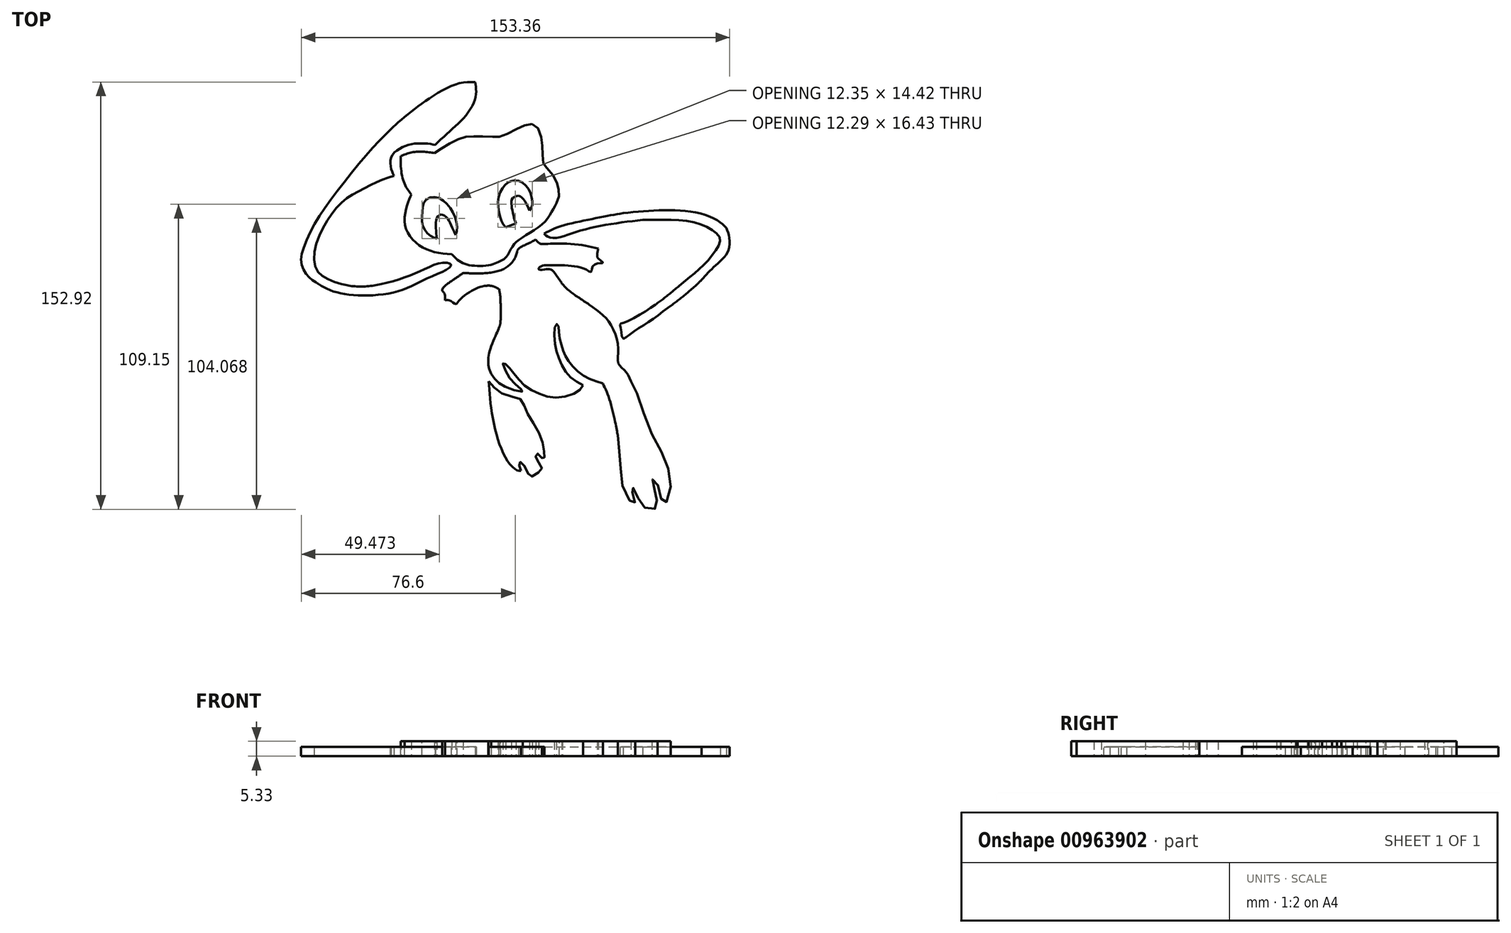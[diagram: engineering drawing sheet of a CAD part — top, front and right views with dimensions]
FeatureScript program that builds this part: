
annotation { "Feature Type Name" : "Feature", "Feature Type Description" : "" }
export const myFeature = defineFeature(function(context is Context, id is Id, definition is map)
    precondition{}
    {
        {
            var Q0;
            Q0=qCreatedBy(makeId("Top.planeOp"),FACE);
            var sketch = newSketch(context, id + "F0", { "sketchPlane" : qUnion([Q0])});
            skFitSpline(sketch, "E0", {"points": [v(-36.88, 36.08) * mm, v(-38.4, 38.25) * mm, v(-40.15, 42.6) * mm, v(-40.65, 48.33) * mm, v(-40.58, 49.85) * mm], "startDerivative": vector(-6.94, 9.09) * mm, "endDerivative": vector(0.6, 7.48) * mm});
            skFitSpline(sketch, "E1", {"points": [v(-40.58, 49.85) * mm, v(-38.04, 50.8) * mm, v(-34.93, 51.37) * mm, v(-31.38, 51.3) * mm, v(-28.55, 50.87) * mm], "startDerivative": vector(10.5, 4.31) * mm, "endDerivative": vector(11.28, -2.04) * mm});
            skFitSpline(sketch, "E2", {"points": [v(-28.55, 50.87) * mm, v(-24.87, 53.3) * mm, v(-19.99, 55.88) * mm, v(-16.36, 56.8) * mm, v(-12.2, 56.87) * mm, v(-6.98, 56.74) * mm, v(-4.41, 57) * mm, v(1, 59.57) * mm, v(4.83, 61.1) * mm, v(7.67, 60.76) * mm, v(9.65, 56.27) * mm, v(10.11, 52.11) * mm, v(10.44, 47.3) * mm, v(11.57, 45.71) * mm, v(14.54, 41.82) * mm, v(15.6, 38.91) * mm, v(16.05, 35.8) * mm, v(15.13, 32.97) * mm], "startDerivative": vector(55.8, 38.5) * mm, "endDerivative": vector(-24.9, -54.1) * mm});
            skFitSpline(sketch, "E3", {"points": [v(15.13, 32.97) * mm, v(13.23, 29.5) * mm, v(9.9, 25.32) * mm, v(3.54, 21.13) * mm, v(0, 18.38) * mm, v(-1.7, 15.62) * mm, v(-3.4, 13.15) * mm, v(-5.2, 12.2) * mm], "startDerivative": vector(-12.69, -24.26) * mm, "endDerivative": vector(-18.67, -6.95) * mm});
            skFitSpline(sketch, "E4", {"points": [v(-5.2, 12.2) * mm, v(-8.38, 10.92) * mm, v(-15.27, 10.68) * mm, v(-19.62, 12.2) * mm, v(-22.36, 14.64) * mm], "startDerivative": vector(-12.64, -6.7) * mm, "endDerivative": vector(-11.41, 11.76) * mm});
            skFitSpline(sketch, "E5", {"points": [v(-22.36, 14.64) * mm, v(-29.1, 15.62) * mm, v(-34.66, 18.38) * mm, v(-38.53, 23.3) * mm, v(-39.1, 28.91) * mm, v(-37.75, 33.9) * mm, v(-36.88, 36.08) * mm], "startDerivative": vector(-36.55, 3.17) * mm, "endDerivative": vector(7.3, 17.53) * mm});
            skFitSpline(sketch, "E6", {"points": [v(-27.74, 20.26) * mm, v(-28, 23.55) * mm, v(-27.97, 26.8) * mm, v(-27.14, 28.47) * mm, v(-25.9, 28.88) * mm, v(-24.15, 27.82) * mm, v(-22.83, 25.7) * mm, v(-21.65, 22.95) * mm, v(-20.94, 21.55) * mm], "startDerivative": vector(-1.85, 21.58) * mm, "endDerivative": vector(6.7, -12.08) * mm});
            skFitSpline(sketch, "E7", {"points": [v(-20.94, 21.55) * mm, v(-20.44, 24.42) * mm, v(-21.43, 28.58) * mm, v(-23.73, 32.29) * mm, v(-27.18, 34.9) * mm, v(-30.4, 34.9) * mm, v(-32.4, 32.97) * mm, v(-32.96, 29.53) * mm, v(-32.93, 25.74) * mm, v(-31.6, 22.72) * mm, v(-29.48, 20.98) * mm, v(-27.74, 20.26) * mm], "startDerivative": vector(8.86, 31.93) * mm, "endDerivative": vector(24.92, -8.61) * mm});
            skLineSegment(sketch, "E8", {"start": v(0.64, 25.77) * mm, "end": v(-3.1, 24.33) * mm});
            skFitSpline(sketch, "E9", {"points": [v(-3.1, 24.33) * mm, v(-4.7, 26.86) * mm, v(-5.73, 31.34) * mm, v(-5.33, 36.17) * mm, v(-3.1, 39.67) * mm, v(-0.97, 40.88) * mm, v(1.96, 40.82) * mm, v(4.95, 38.23) * mm, v(6.27, 34.79) * mm, v(6.39, 32.09) * mm, v(5.4, 30.37) * mm], "startDerivative": vector(-18.53, 24.2) * mm, "endDerivative": vector(-15.72, -20.8) * mm});
            skFitSpline(sketch, "E10", {"points": [v(5.4, 30.37) * mm, v(4.03, 33.3) * mm, v(2.36, 35.3) * mm, v(1.16, 35.6) * mm, v(-0.68, 34.67) * mm, v(-1.02, 32.66) * mm, v(-0.68, 30.37) * mm, v(0, 27.55) * mm, v(0.64, 25.77) * mm], "startDerivative": vector(-8.23, 19.96) * mm, "endDerivative": vector(5.68, -14.34) * mm});
            skFitSpline(sketch, "E11", {"points": [v(-28.3, 53.85) * mm, v(-22.62, 59.17) * mm, v(-17.41, 64.25) * mm, v(-14.15, 69.88) * mm, v(-13.66, 73.45) * mm, v(-13.97, 76.31) * mm], "startDerivative": vector(23.72, 22.62) * mm, "endDerivative": vector(-2.81, 19.35) * mm});
            skFitSpline(sketch, "E12", {"points": [v(-13.97, 76.31) * mm, v(-19.11, 76) * mm, v(-25.25, 73.58) * mm, v(-32.16, 69.26) * mm, v(-37.13, 65.53) * mm, v(-41.53, 61.88) * mm, v(-44.08, 59.5) * mm], "startDerivative": vector(-32.41, 0.3) * mm, "endDerivative": vector(-18.17, -17.44) * mm});
            skFitSpline(sketch, "E13", {"points": [v(-44.08, 59.5) * mm, v(-51.8, 51.48) * mm, v(-63.2, 37.48) * mm, v(-71.34, 25.77) * mm, v(-75.54, 16.64) * mm, v(-76.22, 11.77) * mm, v(-74.95, 8.38) * mm, v(-73.1, 6.15) * mm, v(-70.98, 4.61) * mm], "startDerivative": vector(-48.4, -47.85) * mm, "endDerivative": vector(29.7, -19.4) * mm});
            skFitSpline(sketch, "E14", {"points": [v(-70.98, 4.61) * mm, v(-65.73, 1.76) * mm, v(-56.11, 0) * mm, v(-41.53, 1.5) * mm, v(-30.47, 6.38) * mm, v(-23.8, 9.45) * mm, v(-22.65, 11) * mm, v(-25.86, 11.63) * mm, v(-32.16, 9.32) * mm, v(-40.09, 6.12) * mm, v(-50.09, 3.56) * mm, v(-58.94, 3.43) * mm, v(-66.88, 5.86) * mm, v(-70.98, 9.58) * mm, v(-70.98, 17.91) * mm, v(-66.24, 27.79) * mm, v(-60.86, 34.07) * mm, v(-54.7, 37.79) * mm, v(-48.55, 40.86) * mm, v(-43.04, 42.79) * mm], "startDerivative": vector(103.96, -66.84) * mm, "endDerivative": vector(119.1, 36.89) * mm});
            skFitSpline(sketch, "E15", {"points": [v(-43.04, 42.79) * mm, v(-44.08, 45.32) * mm, v(-44.08, 49.34) * mm, v(-41, 52.5) * mm, v(-36.55, 54.15) * mm, v(-31.3, 54.3) * mm, v(-28.3, 53.85) * mm], "startDerivative": vector(-8.33, 16.7) * mm, "endDerivative": vector(18.9, -3.53) * mm});
            skFitSpline(sketch, "E16", {"points": [v(7.73, 19.96) * mm, v(4.7, 18.38) * mm, v(1.47, 16.59) * mm, v(0.64, 14.22) * mm, v(-1.21, 11.37) * mm, v(-4.34, 9.18) * mm, v(-10.33, 7.93) * mm, v(-15.9, 7.9) * mm, v(-18.3, 8) * mm], "startDerivative": vector(-23.75, -13.65) * mm, "endDerivative": vector(-21.58, 1.02) * mm});
            skFitSpline(sketch, "E17", {"points": [v(-18.3, 8) * mm, v(-21.48, 5.79) * mm, v(-25.73, 2.22) * mm, v(-25.51, 1.24) * mm, v(-24.96, 0.69) * mm, v(-24.75, -0.76) * mm, v(-24.75, -1.78) * mm], "startDerivative": vector(-11.77, -8.3) * mm, "endDerivative": vector(-0.07, -7.72) * mm});
            skFitSpline(sketch, "E18", {"points": [v(-24.75, -1.78) * mm, v(-23.18, -1.78) * mm, v(-20.94, -3.12) * mm, v(-19.7, -1.78) * mm, v(-15.31, 1.57) * mm, v(-11.82, 3.08) * mm, v(-8.28, 3.4) * mm, v(-5.41, 2.2) * mm], "startDerivative": vector(14.29, 3.8) * mm, "endDerivative": vector(18.83, -10.57) * mm});
            skFitSpline(sketch, "E19", {"points": [v(-5.41, -11.46) * mm, v(-6.46, -13.9) * mm, v(-8.5, -18.88) * mm, v(-9.27, -22.77) * mm, v(-9.19, -25.46) * mm, v(-8.23, -28.1) * mm], "startDerivative": vector(-5.21, -12.45) * mm, "endDerivative": vector(6.45, -14.59) * mm});
            skFitSpline(sketch, "E20", {"points": [v(-5.41, -11.46) * mm, v(-5.02, -10.14) * mm, v(-4.86, -5.9) * mm, v(-5.02, -0.37) * mm, v(-5.41, 2.2) * mm], "startDerivative": vector(2.76, 6.94) * mm, "endDerivative": vector(-2.02, 10.26) * mm});
            skFitSpline(sketch, "E21", {"points": [v(-8.23, -28.1) * mm, v(-6.3, -30.62) * mm, v(-2.7, -32.95) * mm, v(3.02, -34.4) * mm, v(1.33, -32.7) * mm, v(-2.6, -28.1) * mm, v(-3.98, -24.1) * mm, v(-2.53, -25.15) * mm, v(0, -28.1) * mm, v(3.82, -32.39) * mm, v(9.45, -35.44) * mm, v(15.89, -36.57) * mm, v(22.56, -34.56) * mm, v(24.65, -32.14) * mm], "startDerivative": vector(28.07, -40.83) * mm, "endDerivative": vector(24.08, 39.06) * mm});
            skFitSpline(sketch, "E22", {"points": [v(24.65, -32.14) * mm, v(19.46, -28.61) * mm, v(16.04, -22.68) * mm, v(14.52, -16.3) * mm, v(14.9, -10.44) * mm, v(15.66, -10.59) * mm, v(15.96, -13.48) * mm, v(17.1, -18.5) * mm, v(18.55, -22.07) * mm, v(21.74, -26.25) * mm, v(26.3, -29.6) * mm, v(31.7, -31.5) * mm], "startDerivative": vector(-53.5, 28.4) * mm, "endDerivative": vector(55.72, -15.9) * mm});
            skFitSpline(sketch, "E23", {"points": [v(31.7, -31.5) * mm, v(33.83, -36.52) * mm, v(35.88, -44.2) * mm, v(36.72, -48.3) * mm, v(37.03, -50.06) * mm], "startDerivative": vector(8, -16.8) * mm, "endDerivative": vector(1.73, -10.31) * mm});
            skFitSpline(sketch, "E24", {"points": [v(37.03, -50.06) * mm, v(37.67, -56.88) * mm, v(38.28, -65.1) * mm, v(40.12, -71.84) * mm, v(43.18, -74.9) * mm, v(43.1, -73.5) * mm, v(42.4, -70.97) * mm, v(41.78, -68.6) * mm, v(42.74, -69.04) * mm, v(44.05, -72.02) * mm, v(46.24, -75.6) * mm, v(48.43, -76.56) * mm, v(50.96, -76.04) * mm, v(51.14, -73.77) * mm, v(50.44, -70) * mm, v(49.3, -67.03) * mm, v(49.65, -65.8) * mm, v(50.96, -67.03) * mm, v(52.28, -70.88) * mm, v(53.41, -74.73) * mm, v(55.25, -72.45) * mm, v(55.69, -64.58) * mm, v(52.89, -56.53) * mm, v(48, -46.82) * mm, v(43.88, -35.1) * mm, v(41.78, -30.72) * mm], "startDerivative": vector(13.24, -128.19) * mm, "endDerivative": vector(-47.37, 85.69) * mm});
            skFitSpline(sketch, "E25", {"points": [v(41.78, -30.72) * mm, v(39.73, -27.08) * mm, v(37.25, -24.41) * mm, v(37.25, -19.83) * mm, v(34.98, -11.16) * mm, v(30.4, -6) * mm, v(23.99, -1.41) * mm, v(17.4, 3.84) * mm, v(13.4, 9.09) * mm, v(11.07, 9.25) * mm, v(8.74, 9.34) * mm, v(9.57, 10.42) * mm, v(12.82, 10.75) * mm, v(17.74, 10.75) * mm, v(21.82, 10.34) * mm, v(25.32, 9.42) * mm, v(27.49, 8.42) * mm, v(27.82, 9.75) * mm, v(29.73, 11.34) * mm, v(31.7, 11.67) * mm, v(30.07, 13.17) * mm], "startDerivative": vector(-32.27, 75.78) * mm, "endDerivative": vector(-69.54, 49.62) * mm});
            skFitSpline(sketch, "E26", {"points": [v(30.07, 13.17) * mm, v(29.68, 13.9) * mm, v(30.07, 16.7) * mm], "startDerivative": vector(-1.4, 1.7) * mm, "endDerivative": vector(1.15, 5.02) * mm});
            skFitSpline(sketch, "E27", {"points": [v(30.07, 16.7) * mm, v(22.73, 18.2) * mm, v(13.95, 18.48) * mm, v(10.79, 18.39) * mm, v(9.05, 18.57) * mm, v(7.73, 19.96) * mm], "startDerivative": vector(-25.6, 6.72) * mm, "endDerivative": vector(-8.87, 12.5) * mm});
            skFitSpline(sketch, "E28", {"points": [v(2.36, -62.8) * mm, v(0.76, -62.5) * mm, v(-2.57, -59) * mm, v(-6.3, -50.06) * mm, v(-8.47, -38.73) * mm, v(-9.1, -30.72) * mm], "startDerivative": vector(-15.3, 0.2) * mm, "endDerivative": vector(-2, 34.43) * mm});
            skFitSpline(sketch, "E29", {"points": [v(-9.1, -30.72) * mm, v(-6.83, -33.36) * mm, v(-2.86, -35.76) * mm, v(1.7, -36.87) * mm, v(3.27, -38.68) * mm, v(4.67, -42.12) * mm, v(7.73, -47.26) * mm, v(9.98, -52.26) * mm, v(10.68, -55.72) * mm, v(10.74, -57.77) * mm, v(10.68, -58.76) * mm, v(9.52, -57.7) * mm, v(8.4, -56.66) * mm, v(7.73, -56.9) * mm, v(7.73, -58) * mm, v(9, -60.22) * mm, v(9.87, -61.8) * mm, v(9.4, -62.79) * mm, v(7, -64.42) * mm, v(5.66, -64.95) * mm, v(4.55, -62.96) * mm, v(3.15, -60.4) * mm, v(2.1, -59.64) * mm, v(1.63, -60.1) * mm, v(1.87, -61.39) * mm, v(2.36, -62.8) * mm], "startDerivative": vector(41.4, -54) * mm, "endDerivative": vector(14.87, -42.66) * mm});
            skFitSpline(sketch, "E30", {"points": [v(10.72, 22.02) * mm, v(15.3, 24.28) * mm, v(23.56, 26.44) * mm, v(32.84, 28.33) * mm, v(38.94, 29.4) * mm], "startDerivative": vector(20, 11.39) * mm, "endDerivative": vector(24.9, 4.23) * mm});
            skFitSpline(sketch, "E31", {"points": [v(10.72, 22.02) * mm, v(12.02, 21) * mm, v(14.93, 20.56) * mm, v(20, 22.02) * mm, v(27.23, 24.07) * mm, v(36.57, 25.8) * mm, v(46, 27.03) * mm], "startDerivative": vector(12.39, -12.48) * mm, "endDerivative": vector(43.26, 5.28) * mm});
            skFitSpline(sketch, "E32", {"points": [v(46, 27.03) * mm, v(54.46, 27.03) * mm, v(64.58, 26.06) * mm, v(71.34, 23.07) * mm, v(73.7, 20) * mm, v(72.38, 16.45) * mm, v(68.06, 11.1) * mm, v(62.98, 6.64) * mm, v(59.01, 3.36) * mm], "startDerivative": vector(56.72, 0.57) * mm, "endDerivative": vector(-34.14, -28.32) * mm});
            skFitSpline(sketch, "E33", {"points": [v(38.94, 29.4) * mm, v(48.57, 30.24) * mm, v(58.73, 30.38) * mm, v(68.13, 28.85) * mm, v(73.84, 26.06) * mm, v(75.93, 24.11) * mm], "startDerivative": vector(41.77, 4.1) * mm, "endDerivative": vector(14.3, -15.48) * mm});
            skFitSpline(sketch, "E34", {"points": [v(59.01, 3.36) * mm, v(52.8, -1.66) * mm, v(46, -6.28) * mm, v(38.94, -9.92) * mm, v(37.93, -10.28) * mm, v(38.17, -12.05) * mm, v(38.94, -15.45) * mm, v(41.63, -13.75) * mm, v(47.58, -9.92) * mm, v(54.08, -5.19) * mm, v(60.39, -0.45) * mm, v(67.07, 5.5) * mm], "startDerivative": vector(-56.72, -47.28) * mm, "endDerivative": vector(57.6, 53.68) * mm});
            skFitSpline(sketch, "E35", {"points": [v(67.07, 5.5) * mm, v(71.5, 10.15) * mm, v(76.76, 16.45) * mm, v(75.93, 24.11) * mm], "startDerivative": vector(12.97, 14.55) * mm, "endDerivative": vector(-7.34, 15.71) * mm});
            skCircle(sketch, "E36", {"center": v(3.64, 0.36) * mm, "radius": 102.9 * mm});
            skArc(sketch, "E37", {"start": v(17.07, 4.01) * mm, "mid": v(15.47, 7.68) * mm, "end": v(12.9, 10.75) * mm});
            skLineSegment(sketch, "E38", {"start": v(-24, 4.01) * mm, "end": v(-35.33, 4.01) * mm});
            skLineSegment(sketch, "E39", {"start": v(17.07, 4.01) * mm, "end": v(59.8, 4.01) * mm});
            skLineSegment(sketch, "E40.MirrorCS", {"start": v(-9.8, -3.3) * mm, "end": v(-99.19, -3.3) * mm});
            skLineSegment(sketch, "E41.MirrorCS", {"start": v(26.78, -3.3) * mm, "end": v(50.57, -3.3) * mm});
            skArc(sketch, "E42", {"start": v(-6.17, 2.6) * mm, "mid": v(-6.28, -1.34) * mm, "end": v(-4.86, -5.02) * mm});
            skArc(sketch, "E43.trimOffspring", {"start": v(0.53, 13.92) * mm, "mid": v(-4.2, 11.86) * mm, "end": v(-7.84, 8.22) * mm});
            skArc(sketch, "E44.trimOffspring", {"start": v(-9.8, 4.01) * mm, "mid": v(-9.6, -3.94) * mm, "end": v(-5.09, -10.49) * mm});
            skLineSegment(sketch, "E45.trimOffspring", {"start": v(56.64, -3.3) * mm, "end": v(106.47, -3.3) * mm});
            skLineSegment(sketch, "E46.trimOffspring", {"start": v(65.47, 4.01) * mm, "end": v(106.47, 4.01) * mm});
            skLineSegment(sketch, "E47.trimOffspring", {"start": v(-47.61, 4.01) * mm, "end": v(-61.82, 4.01) * mm});
            skLineSegment(sketch, "E48.trimOffspring", {"start": v(-70.04, 4.01) * mm, "end": v(-99.19, 4.01) * mm});
            skText(sketch, "E49", { "text": "Mew\n", "fontName": "OpenSans-Regular.ttf"});
            const initialGuessF0  = {"E49": [-0.09161, -0.03188, 1, 0, 0.02467]};
            skSetInitialGuess(sketch, initialGuessF0);
            skSolve(sketch);
        }
        {
            var Q0;
            Q0=makeQuery(id+"F0.imprint","IMPRINT",FACE,{"disambiguationData":[TD([[makeQuery(id+"F0.imprint","IMPRINT",EDGE,{"derivedFrom":sQuery(id+"F0.wireOp",EDGE,"E0")}),-1.0]])]});
            var Q1;
            Q1=makeQuery(id+"F0.imprint","IMPRINT",FACE,{"disambiguationData":[TD([[makeQuery(id+"F0.imprint","IMPRINT",EDGE,{"derivedFrom":sQuery(id+"F0.wireOp",EDGE,"E16")}),1.0]])]});
            extrude(context, id + "F1", {"entities" : qUnion([Q0, Q1]), "depth" : 5.33 * mm});
        }
        {
            var Q0;
            Q0=makeQuery(id+"F0.imprint","IMPRINT",FACE,{"disambiguationData":[TD([[makeQuery(id+"F0.imprint","IMPRINT",EDGE,{"derivedFrom":sQuery(id+"F0.wireOp",EDGE,"E11")}),1.0]])]});
            var Q1;
            Q1=makeQuery(id+"F0.imprint","IMPRINT",FACE,{"disambiguationData":[TD([[makeQuery(id+"F0.imprint","IMPRINT",EDGE,{"derivedFrom":sQuery(id+"F0.wireOp",EDGE,"E28")}),-1.0]])]});
            var Q2;
            Q2=makeQuery(id+"F0.imprint","IMPRINT",FACE,{"disambiguationData":[TD([[makeQuery(id+"F0.imprint","IMPRINT",EDGE,{"derivedFrom":sQuery(id+"F0.wireOp",EDGE,"E30")}),-1.0]])]});
            extrude(context, id + "F2", {"entities" : qUnion([Q0, Q1, Q2]), "depth" : 3.3 * mm});
        }
    });
